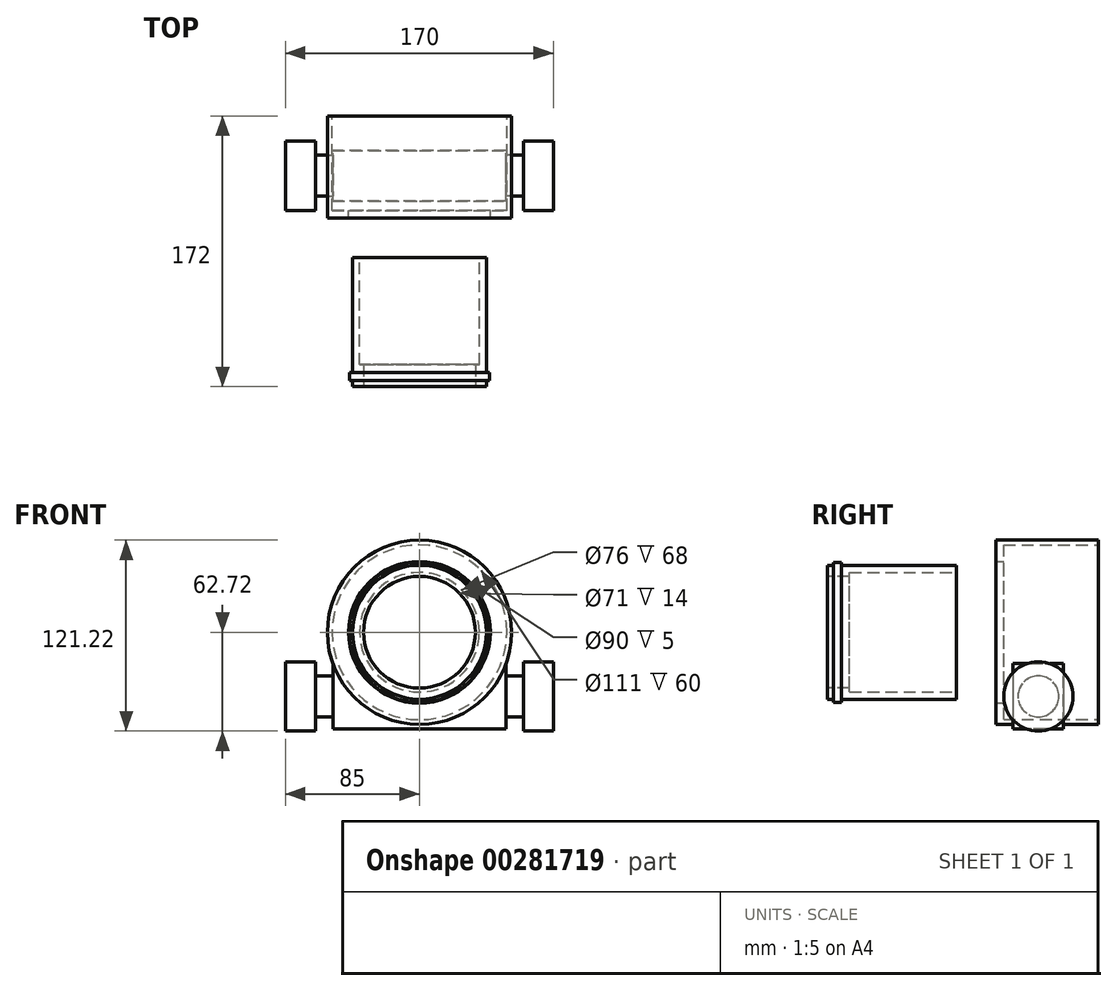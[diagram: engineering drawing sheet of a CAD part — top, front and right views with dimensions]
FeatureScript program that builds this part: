
annotation { "Feature Type Name" : "Feature", "Feature Type Description" : "" }
export const myFeature = defineFeature(function(context is Context, id is Id, definition is map)
    precondition{}
    {
        {
            assignVariable(context, id + "F0", {"name" : "FC_InnerTubeLength", "anyValue" : 82});
        }
        {
            assignVariable(context, id + "F1", {"name" : "FC_InnerTubeFlangeLength", "anyValue" : 14});
        }
        {
            assignVariable(context, id + "F2", {"name" : "FC_InnerTubeFlangeOuterLength", "anyValue" : 9});
        }
        {
            var Q0;
            Q0=qCreatedBy(makeId("Front.planeOp"),FACE);
            var sketch = newSketch(context, id + "F3", { "sketchPlane" : qUnion([Q0])});
            skCircle(sketch, "E0", {"center": v(0, 0) * mm, "radius": 38 * mm});
            skCircle(sketch, "E1", {"center": v(0, 0) * mm, "radius": 43 * mm});
            skCircle(sketch, "E2", {"center": v(0, 0) * mm, "radius": 42.5 * mm});
            skSolve(sketch);
        }
        {
            var Q0;
            Q0=makeQuery(id+"F3.imprint","IMPRINT",FACE,{"disambiguationData":[TD([[makeQuery(id+"F3.imprint","IMPRINT",EDGE,{"derivedFrom":sQuery(id+"F3.wireOp",EDGE,"E0")}),-1.0]])]});
            extrude(context, id + "F4", {"entities" : qUnion([Q0]), "depth" : (getVariable(context, 'FC_InnerTubeLength')) * mm, "offsetDistance" : 25 * mm});
        }
        {
            var Q0;
            Q0=makeQuery(id+"F4.opExtrude","CAP_FACE",FACE,{"disambiguationData":[OSD([sQuery(id+"F3.wireOp",EDGE,"E0"),sQuery(id+"F3.wireOp",EDGE,"E1")])],"isStart":false});
            var sketch = newSketch(context, id + "F5", { "sketchPlane" : qUnion([Q0])});
            skCircle(sketch, "E3", {"center": v(0, 0) * mm, "radius": 44.5 * mm});
            skCircle(sketch, "E4", {"center": v(0, 0) * mm, "radius": 35.5 * mm});
            skCircle(sketch, "E5", {"center": v(0, 0) * mm, "radius": 42.5 * mm});
            skSolve(sketch);
        }
        {
            var Q0;
            Q0=makeQuery(id+"F5.imprint","IMPRINT",FACE,{"disambiguationData":[TD([[makeQuery(id+"F5.imprint","IMPRINT",EDGE,{"derivedFrom":sQuery(id+"F5.wireOp",EDGE,"E4")}),-1.0]])]});
            var Q1;
            Q1=makeQuery(id+"F5.imprint","IMPRINT",FACE,{"disambiguationData":[TD([[makeQuery(id+"F5.imprint","IMPRINT",EDGE,{"derivedFrom":makeQuery(id+"F4.opExtrude","CAP_EDGE",EDGE,{"disambiguationData":[OSD([sQuery(id+"F3.wireOp",EDGE,"E0")])],"isStart":false})}),-1.0]])]});
            extrude(context, id + "F6", {"entities" : qUnion([Q0, Q1]), "operationType" : NewBodyOperationType.ADD, "oppositeDirection" : true, "depth" : (getVariable(context, 'FC_InnerTubeFlangeLength')) * mm, "offsetDistance" : 25 * mm});
        }
        {
            var Q0;
            Q0=makeQuery(id+"F5.imprint","IMPRINT",FACE,{"disambiguationData":[TD([[makeQuery(id+"F5.imprint","IMPRINT",EDGE,{"derivedFrom":sQuery(id+"F5.wireOp",EDGE,"E4")}),-1.0]])]});
            extrude(context, id + "F7", {"entities" : qUnion([Q0]), "operationType" : NewBodyOperationType.ADD, "oppositeDirection" : true, "depth" : (getVariable(context, 'FC_InnerTubeFlangeLength')) * mm, "offsetDistance" : 25 * mm});
        }
        {
            var Q0;
            Q0=makeQuery(id+"F5.imprint","IMPRINT",FACE,{"disambiguationData":[TD([[makeQuery(id+"F5.imprint","IMPRINT",EDGE,{"derivedFrom":sQuery(id+"F5.wireOp",EDGE,"E3")}),1.0]])]});
            extrude(context, id + "F8", {"entities" : qUnion([Q0]), "operationType" : NewBodyOperationType.ADD, "oppositeDirection" : true, "depth" : (getVariable(context, 'FC_InnerTubeFlangeOuterLength')) * mm, "offsetDistance" : 25 * mm});
        }
        {
            var Q0;
            Q0=makeQuery(id+"F5.imprint","IMPRINT",FACE,{"disambiguationData":[TD([[makeQuery(id+"F5.imprint","IMPRINT",EDGE,{"derivedFrom":sQuery(id+"F5.wireOp",EDGE,"E3")}),1.0]])]});
            extrude(context, id + "F9", {"entities" : qUnion([Q0]), "operationType" : NewBodyOperationType.REMOVE, "oppositeDirection" : true, "depth" : 4 * mm, "offsetDistance" : 25 * mm});
        }
        {
            var Q0;
            Q0=qCreatedBy(makeId("Front.planeOp"),FACE);
            cPlane(context, id + "F10", {"entities" : qUnion([Q0]), "cplaneType" : CPlaneType.OFFSET, "offset" : 90 * mm, "oppositeDirection" : true, "width" : 150 * mm, "height" : 150 * mm});
        }
        {
            assignVariable(context, id + "F11", {"name" : "FC_BodyOuterDia", "anyValue" : 117});
        }
        {
            assignVariable(context, id + "F12", {"name" : "FC_BodyLength", "anyValue" : 65});
        }
        {
            var Q0;
            Q0=qCreatedBy(id+"F10.planeOp",FACE);
            var sketch = newSketch(context, id + "F13", { "sketchPlane" : qUnion([Q0])});
            skCircle(sketch, "E6", {"center": v(0, 0) * mm, "radius": 58.5 * mm});
            skCircle(sketch, "E7", {"center": v(0, 0) * mm, "radius": 45 * mm});
            skCircle(sketch, "E8", {"center": v(0, 0) * mm, "radius": 55.5 * mm});
            skSolve(sketch);
        }
        {
            var Q0;
            Q0=makeQuery(id+"F13.imprint","IMPRINT",FACE,{"disambiguationData":[TD([[makeQuery(id+"F13.imprint","IMPRINT",EDGE,{"derivedFrom":sQuery(id+"F13.wireOp",EDGE,"E7")}),-1.0]])]});
            var Q1;
            Q1=makeQuery(id+"F13.imprint","IMPRINT",FACE,{"disambiguationData":[TD([[makeQuery(id+"F13.imprint","IMPRINT",EDGE,{"derivedFrom":sQuery(id+"F13.wireOp",EDGE,"E6")}),1.0]])]});
            extrude(context, id + "F14", {"entities" : qUnion([Q0, Q1]), "depth" : (getVariable(context, 'FC_BodyLength')) * mm, "offsetDistance" : 25 * mm});
        }
        {
            var Q0;
            Q0=makeQuery(id+"F13.imprint","IMPRINT",FACE,{"disambiguationData":[TD([[makeQuery(id+"F13.imprint","IMPRINT",EDGE,{"derivedFrom":sQuery(id+"F13.wireOp",EDGE,"E7")}),-1.0]])]});
            extrude(context, id + "F15", {"entities" : qUnion([Q0]), "operationType" : NewBodyOperationType.REMOVE, "depth" : 60 * mm, "offsetDistance" : 25 * mm});
        }
        {
            var Q0;
            Q0=qCreatedBy(makeId("Top.planeOp"),FACE);
            cPlane(context, id + "F16", {"entities" : qUnion([Q0]), "cplaneType" : CPlaneType.OFFSET, "offset" : (getVariable(context, 'FC_BodyOuterDia') / 2 + 3) * mm, "oppositeDirection" : true, "width" : 150 * mm, "height" : 150 * mm});
        }
        {
            var Q0;
            Q0=qCreatedBy(id+"F16.planeOp",FACE);
            var sketch = newSketch(context, id + "F17", { "sketchPlane" : qUnion([Q0])});
            skLineSegment(sketch, "E9.bottom", {"start": v(55, 68) * mm, "end": v(-55, 68) * mm});
            skLineSegment(sketch, "E9.top", {"start": v(55, 36) * mm, "end": v(-55, 36) * mm});
            skLineSegment(sketch, "E9.left", {"start": v(55, 68) * mm, "end": v(55, 36) * mm});
            skLineSegment(sketch, "E9.right", {"start": v(-55, 68) * mm, "end": v(-55, 36) * mm});
            skPoint(sketch, "E9.middle", {"position": v(0, 52) * mm});
            skSolve(sketch);
        }
        {
            var Q0;
            Q0=makeQuery(id+"F17.imprint","IMPRINT",FACE,{"disambiguationData":[TD([[makeQuery(id+"F17.imprint","IMPRINT",EDGE,{"derivedFrom":sQuery(id+"F17.wireOp",EDGE,"E9.bottom")}),1.0]])]});
            extrude(context, id + "F18", {"entities" : qUnion([Q0]), "operationType" : NewBodyOperationType.ADD, "depth" : 44.8 * mm, "offsetDistance" : 25 * mm});
        }
        {
            var Q0;
            {var subQ2=sQuery(id+"F17.wireOp",EDGE,"E9.bottom");Q0=makeQuery(id+"F18.boolean.opBoolean","SPLIT",FACE,{"disambiguationData":[TD([makeQuery(id+"F14.opExtrude","SWEPT_FACE",FACE,{"disambiguationData":[OSD([sQuery(id+"F13.wireOp",EDGE,"E6")])]})])],"derivedFrom":makeQuery(id+"F18.opExtrude","SWEPT_FACE",FACE,{"disambiguationData":[OSD([subQ2])]})});}
            var sketch = newSketch(context, id + "F19", { "sketchPlane" : qUnion([Q0])});
            skCircle(sketch, "E10", {"center": v(0, 0) * mm, "radius": 55.5 * mm});
            skSolve(sketch);
        }
        {
            var Q0;
            Q0=makeQuery(id+"F19.imprint","IMPRINT",FACE,{"disambiguationData":[TD([[makeQuery(id+"F19.imprint","IMPRINT",EDGE,{"derivedFrom":sQuery(id+"F19.wireOp",EDGE,"E10")}),1.0]])]});
            extrude(context, id + "F20", {"entities" : qUnion([Q0]), "operationType" : NewBodyOperationType.REMOVE, "oppositeDirection" : true, "depth" : 35 * mm, "offsetDistance" : 25 * mm});
        }
        {
            var Q0;
            Q0=makeQuery(id+"F18.opExtrude","SWEPT_FACE",FACE,{"disambiguationData":[OSD([sQuery(id+"F17.wireOp",EDGE,"E9.right")])]});
            var sketch = newSketch(context, id + "F21", { "sketchPlane" : qUnion([Q0])});
            skLineSegment(sketch, "E11", {"start": v(-74.52, -40.72) * mm, "end": v(-36, -40.72) * mm, "construction": true});
            skLineSegment(sketch, "E12", {"start": v(-52, -61.5) * mm, "end": v(-52, -19.93) * mm, "construction": true});
            skCircle(sketch, "E13", {"center": v(-52, -40.72) * mm, "radius": 13 * mm});
            skPoint(sketch, "E13.centerSnap0", {"position": v(-52, -40.72) * mm});
            skSolve(sketch);
        }
        {
            var Q0;
            Q0=makeQuery(id+"F21.imprint","IMPRINT",FACE,{"disambiguationData":[TD([[makeQuery(id+"F21.imprint","IMPRINT",EDGE,{"derivedFrom":sQuery(id+"F21.wireOp",EDGE,"E13")}),1.0]])]});
            extrude(context, id + "F22", {"entities" : qUnion([Q0]), "operationType" : NewBodyOperationType.ADD, "depth" : 30 * mm, "offsetDistance" : 25 * mm});
        }
        {
            var Q0;
            Q0=makeQuery(id+"F22.opExtrude","CAP_FACE",FACE,{"disambiguationData":[OSD([sQuery(id+"F21.wireOp",EDGE,"E13")])],"isStart":false});
            var sketch = newSketch(context, id + "F23", { "sketchPlane" : qUnion([Q0])});
            skCircle(sketch, "E14", {"center": v(-52, -40.72) * mm, "radius": 22 * mm});
            skSolve(sketch);
        }
        {
            var Q0;
            Q0=makeQuery(id+"F23.imprint","IMPRINT",FACE,{"disambiguationData":[TD([[makeQuery(id+"F23.imprint","IMPRINT",EDGE,{"derivedFrom":sQuery(id+"F23.wireOp",EDGE,"E14")}),1.0]])]});
            extrude(context, id + "F24", {"entities" : qUnion([Q0]), "operationType" : NewBodyOperationType.ADD, "oppositeDirection" : true, "depth" : 19 * mm, "offsetDistance" : 25 * mm});
        }
        {
            var Q0;
            Q0=makeQuery(id+"F18.opExtrude","SWEPT_FACE",FACE,{"disambiguationData":[OSD([sQuery(id+"F17.wireOp",EDGE,"E9.left")])]});
            var sketch = newSketch(context, id + "F25", { "sketchPlane" : qUnion([Q0])});
            skLineSegment(sketch, "E15", {"start": v(52, -19.93) * mm, "end": v(52, -67.02) * mm, "construction": true});
            skLineSegment(sketch, "E16", {"start": v(36, -40.72) * mm, "end": v(76.48, -40.72) * mm, "construction": true});
            skCircle(sketch, "E17", {"center": v(52, -40.72) * mm, "radius": 13 * mm});
            skSolve(sketch);
        }
        {
            var Q0;
            Q0=makeQuery(id+"F25.imprint","IMPRINT",FACE,{"disambiguationData":[TD([[makeQuery(id+"F25.imprint","IMPRINT",EDGE,{"derivedFrom":sQuery(id+"F25.wireOp",EDGE,"E17")}),1.0]])]});
            extrude(context, id + "F26", {"entities" : qUnion([Q0]), "operationType" : NewBodyOperationType.ADD, "depth" : 30 * mm, "offsetDistance" : 25 * mm});
        }
        {
            var Q0;
            Q0=makeQuery(id+"F26.opExtrude","CAP_FACE",FACE,{"disambiguationData":[OSD([sQuery(id+"F25.wireOp",EDGE,"E17")])],"isStart":false});
            var sketch = newSketch(context, id + "F27", { "sketchPlane" : qUnion([Q0])});
            skCircle(sketch, "E18", {"center": v(52, -40.72) * mm, "radius": 22 * mm});
            skSolve(sketch);
        }
        {
            var Q0;
            Q0=makeQuery(id+"F27.imprint","IMPRINT",FACE,{"disambiguationData":[TD([[makeQuery(id+"F27.imprint","IMPRINT",EDGE,{"derivedFrom":makeQuery(id+"F26.opExtrude","CAP_EDGE",EDGE,{"disambiguationData":[OSD([sQuery(id+"F25.wireOp",EDGE,"E17")])],"isStart":false})}),1.0]])]});
            var Q1;
            Q1=makeQuery(id+"F27.imprint","IMPRINT",FACE,{"disambiguationData":[TD([[makeQuery(id+"F27.imprint","IMPRINT",EDGE,{"derivedFrom":sQuery(id+"F27.wireOp",EDGE,"E18")}),1.0]])]});
            extrude(context, id + "F28", {"entities" : qUnion([Q0, Q1]), "operationType" : NewBodyOperationType.ADD, "oppositeDirection" : true, "depth" : 19 * mm, "offsetDistance" : 25 * mm});
        }
    });
